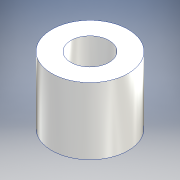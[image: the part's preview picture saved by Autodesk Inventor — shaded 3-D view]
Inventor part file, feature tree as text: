
AUTODESK INVENTOR PART (.ipt)
format: ipt  version: 2020.2 (Build 242310000, 310)  size: 105,472 bytes
history: native  units: mm
features: other x1, extrude x1, sketch x1
ambient origin geometry x8: Origin, YZ Plane, XZ Plane, XY Plane, X Axis, Y Axis, Z Axis, Center Point
bodies: Body1 (feature_tree)
feature tree (3):
  other  "ソリッド1"
  extrude  "押し出し1"  Depth=4.0mm
  sketch  "スケッチ1"
